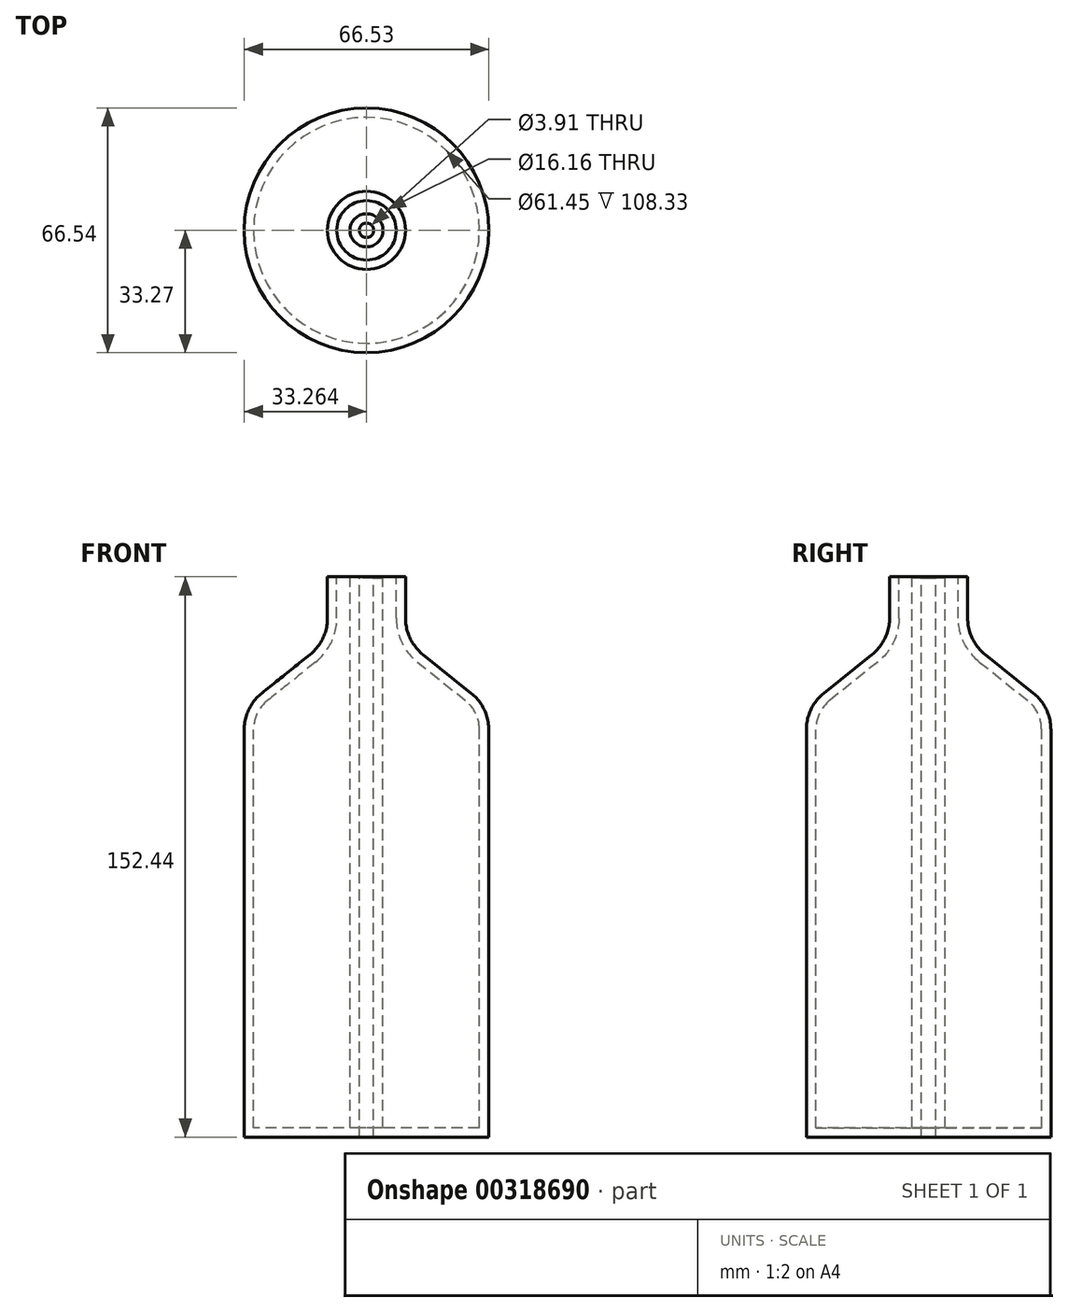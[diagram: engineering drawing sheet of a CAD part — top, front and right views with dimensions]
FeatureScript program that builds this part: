
annotation { "Feature Type Name" : "Feature", "Feature Type Description" : "" }
export const myFeature = defineFeature(function(context is Context, id is Id, definition is map)
    precondition{}
    {
        {
            var Q0;
            Q0=qCreatedBy(makeId("Front.planeOp"),FACE);
            var sketch = newSketch(context, id + "F0", { "sketchPlane" : qUnion([Q0])});
            skLineSegment(sketch, "E0", {"start": v(0, 76.02) * mm, "end": v(0, -76.04) * mm});
            skLineSegment(sketch, "E1", {"start": v(0, -76.04) * mm, "end": v(-31.31, -76.04) * mm});
            skLineSegment(sketch, "E2", {"start": v(-31.31, -76.04) * mm, "end": v(-31.31, 40.93) * mm});
            skLineSegment(sketch, "E3", {"start": v(-31.31, 40.93) * mm, "end": v(-8.67, 59.04) * mm});
            skLineSegment(sketch, "E4", {"start": v(-8.67, 59.04) * mm, "end": v(-8.67, 76.4) * mm});
            skLineSegment(sketch, "E5", {"start": v(-8.67, 76.4) * mm, "end": v(0, 76.02) * mm});
            skSolve(sketch);
        }
        {
            var Q0;
            Q0=makeQuery(id+"F0.imprint","IMPRINT",FACE,{"disambiguationData":[TD([[makeQuery(id+"F0.imprint","IMPRINT",EDGE,{"derivedFrom":sQuery(id+"F0.wireOp",EDGE,"E0")}),-1.0]])]});
            var sketch = newSketch(context, id + "F1", { "sketchPlane" : qUnion([Q0])});
            skLineSegment(sketch, "E6", {"start": v(0, 76.02) * mm, "end": v(0, -76.42) * mm, "construction": true});
            skLineSegment(sketch, "E7", {"start": v(1.95, 76.02) * mm, "end": v(1.95, -76.33) * mm});
            skSolve(sketch);
        }
        {
            var Q0;
            Q0 = qSketchRegion(id + "F1", true);
            var Q1;
            Q1=makeQuery(id+"F0.imprint","IMPRINT",FACE,{"disambiguationData":[TD([[makeQuery(id+"F0.imprint","IMPRINT",EDGE,{"derivedFrom":sQuery(id+"F0.wireOp",EDGE,"E0")}),-1.0]])]});
            var Q2;
            Q2=sQuery(id+"F1.wireOp",EDGE,"E7");
            revolve(context, id + "F2", {"entities" : qUnion([Q0, Q1]), "axis" : qUnion([Q2]), "revolveType" : RevolveType.FULL});
        }
        {
            var Q0;
            Q0=makeQuery(id+"F2.opRevolve","SWEPT_EDGE",EDGE,{"disambiguationData":[OSD([sQuery(id+"F0.wireOp",EDGE,"E2"),sQuery(id+"F0.wireOp",EDGE,"E3")])]});
            var Q1;
            Q1=makeQuery(id+"F2.opRevolve","SWEPT_EDGE",EDGE,{"disambiguationData":[OSD([sQuery(id+"F0.wireOp",EDGE,"E3"),sQuery(id+"F0.wireOp",EDGE,"E4")])]});
            fillet(context, id + "F3", {"entities" : qUnion([Q0, Q1]), "radius" : 12.7 * mm, "tangentPropagation" : true, "allowEdgeOverflow" : false});
        }
        {
            var Q0;
            Q0=makeQuery(id+"F2.opRevolve","SWEPT_FACE",FACE,{"disambiguationData":[OSD([sQuery(id+"F0.wireOp",EDGE,"E5")])]});
            shell(context, id + "F4", {"entities" : qUnion([Q0]), "thickness" : 2.54 * mm});
        }
    });
